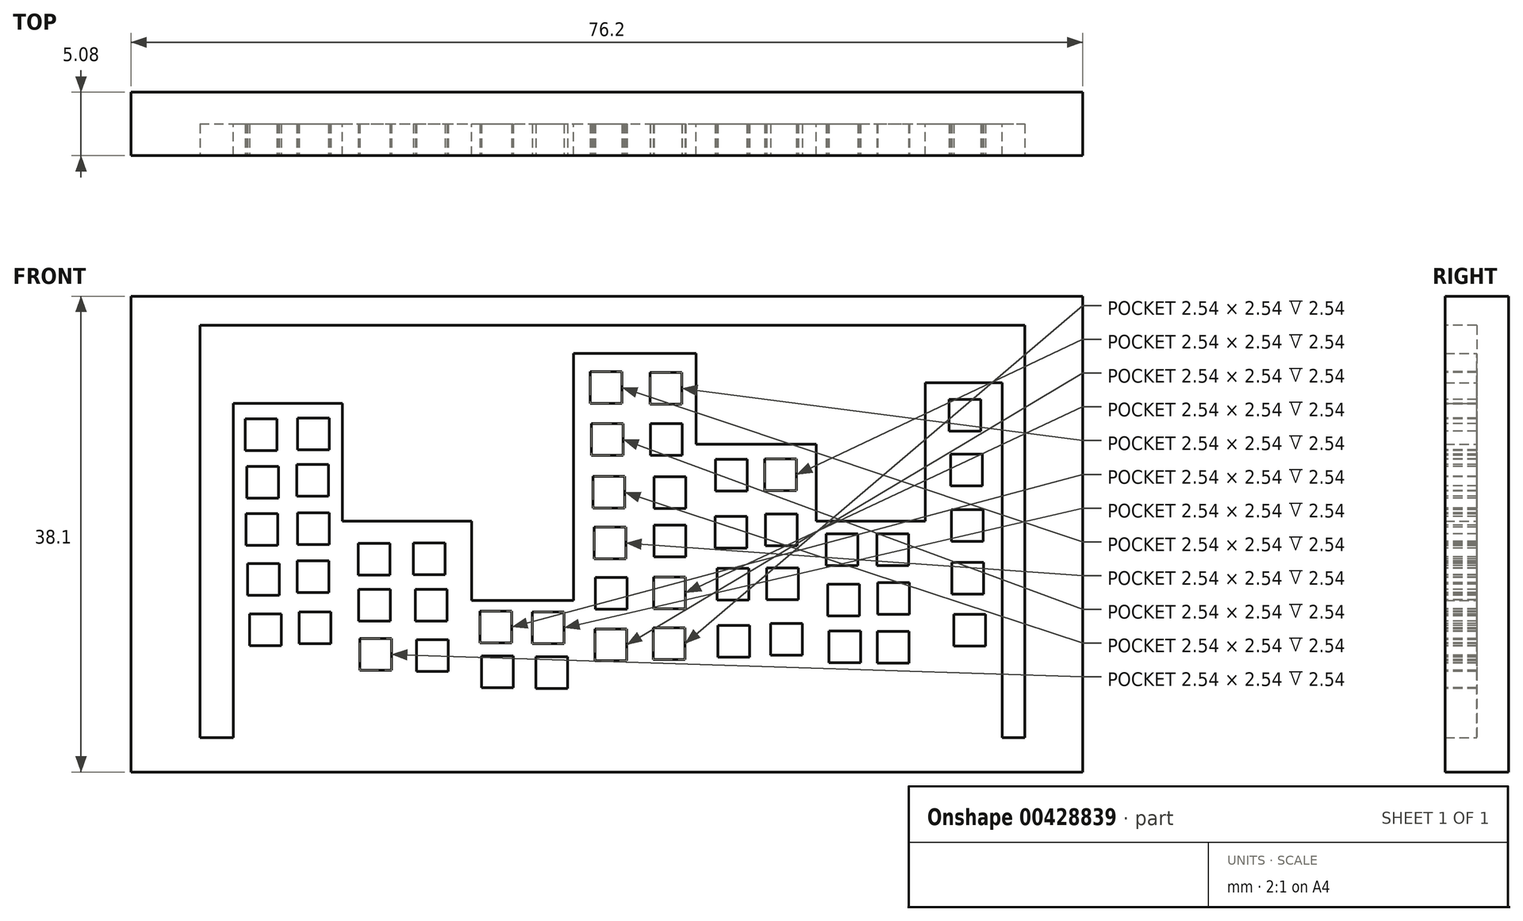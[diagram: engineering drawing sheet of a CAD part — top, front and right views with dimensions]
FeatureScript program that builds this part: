
annotation { "Feature Type Name" : "Feature", "Feature Type Description" : "" }
export const myFeature = defineFeature(function(context is Context, id is Id, definition is map)
    precondition{}
    {
        {
            var Q0;
            Q0=qCreatedBy(makeId("Front.planeOp"),FACE);
            var sketch = newSketch(context, id + "F0", { "sketchPlane" : qUnion([Q0])});
            skLineSegment(sketch, "E0.bottom", {"start": v(0, 0) * mm, "end": v(76.2, 0) * mm});
            skLineSegment(sketch, "E0.top", {"start": v(0, -38.1) * mm, "end": v(76.2, -38.1) * mm});
            skLineSegment(sketch, "E0.left", {"start": v(0, 0) * mm, "end": v(0, -38.1) * mm});
            skLineSegment(sketch, "E0.right", {"start": v(76.2, 0) * mm, "end": v(76.2, -38.1) * mm});
            skSolve(sketch);
        }
        {
            var Q0;
            Q0 = qSketchRegion(id + "F0", true);
            extrude(context, id + "F1", {"entities" : qUnion([Q0]), "depth" : 5.08 * mm});
        }
        {
            var Q0;
            Q0=makeQuery(id+"F1.opExtrude","CAP_FACE",FACE,{"disambiguationData":[OSD([sQuery(id+"F0.wireOp",EDGE,"E0.bottom"),sQuery(id+"F0.wireOp",EDGE,"E0.top"),sQuery(id+"F0.wireOp",EDGE,"E0.left"),sQuery(id+"F0.wireOp",EDGE,"E0.right")])],"isStart":false});
            var sketch = newSketch(context, id + "F2", { "sketchPlane" : qUnion([Q0])});
            skLineSegment(sketch, "E1.bottom", {"start": v(5.51, -2.33) * mm, "end": v(71.55, -2.33) * mm});
            skLineSegment(sketch, "E1.top", {"start": v(5.51, -35.35) * mm, "end": v(71.55, -35.35) * mm});
            skLineSegment(sketch, "E1.left", {"start": v(5.51, -2.33) * mm, "end": v(5.51, -35.35) * mm});
            skLineSegment(sketch, "E1.right", {"start": v(71.55, -2.33) * mm, "end": v(71.55, -35.35) * mm});
            skSolve(sketch);
        }
        {
            var Q0;
            Q0 = qSketchRegion(id + "F2", true);
            extrude(context, id + "F3", {"entities" : qUnion([Q0]), "operationType" : NewBodyOperationType.REMOVE, "oppositeDirection" : true, "depth" : 2.54 * mm});
        }
        {
            var Q0;
            Q0=makeQuery(id+"F3.boolean.opBoolean","COPY",FACE,{"derivedFrom":makeQuery(id+"F3.opExtrude","CAP_FACE",FACE,{"disambiguationData":[OSD([sQuery(id+"F2.wireOp",EDGE,"E1.bottom"),sQuery(id+"F2.wireOp",EDGE,"E1.top"),sQuery(id+"F2.wireOp",EDGE,"E1.left"),sQuery(id+"F2.wireOp",EDGE,"E1.right")])],"isStart":false})});
            var sketch = newSketch(context, id + "F4", { "sketchPlane" : qUnion([Q0])});
            skLineSegment(sketch, "E2.bottom", {"start": v(8.2, -35.35) * mm, "end": v(16.9, -35.35) * mm});
            skLineSegment(sketch, "E2.top", {"start": v(8.2, -8.57) * mm, "end": v(16.9, -8.57) * mm});
            skLineSegment(sketch, "E2.left", {"start": v(8.2, -35.35) * mm, "end": v(8.2, -8.57) * mm});
            skLineSegment(sketch, "E2.right", {"start": v(16.9, -35.35) * mm, "end": v(16.9, -8.57) * mm});
            skLineSegment(sketch, "E3.bottom", {"start": v(16.9, -18.01) * mm, "end": v(27.26, -18.01) * mm});
            skLineSegment(sketch, "E3.top", {"start": v(16.9, -35.35) * mm, "end": v(27.26, -35.35) * mm});
            skLineSegment(sketch, "E3.left", {"start": v(16.9, -18.01) * mm, "end": v(16.9, -35.35) * mm});
            skLineSegment(sketch, "E3.right", {"start": v(27.26, -18.01) * mm, "end": v(27.26, -35.35) * mm});
            skLineSegment(sketch, "E4.bottom", {"start": v(27.26, -24.37) * mm, "end": v(35.43, -24.37) * mm});
            skLineSegment(sketch, "E4.top", {"start": v(27.26, -35.35) * mm, "end": v(35.43, -35.35) * mm});
            skLineSegment(sketch, "E4.left", {"start": v(27.26, -24.37) * mm, "end": v(27.26, -35.35) * mm});
            skLineSegment(sketch, "E4.right", {"start": v(35.43, -24.37) * mm, "end": v(35.43, -35.35) * mm});
            skLineSegment(sketch, "E5.bottom", {"start": v(35.43, -35.35) * mm, "end": v(45.24, -35.35) * mm});
            skLineSegment(sketch, "E5.top", {"start": v(35.43, -4.57) * mm, "end": v(45.24, -4.57) * mm});
            skLineSegment(sketch, "E5.left", {"start": v(35.43, -35.35) * mm, "end": v(35.43, -4.57) * mm});
            skLineSegment(sketch, "E5.right", {"start": v(45.24, -35.35) * mm, "end": v(45.24, -4.57) * mm});
            skLineSegment(sketch, "E6.bottom", {"start": v(45.24, -35.35) * mm, "end": v(54.86, -35.35) * mm});
            skLineSegment(sketch, "E6.top", {"start": v(45.24, -11.84) * mm, "end": v(54.86, -11.84) * mm});
            skLineSegment(sketch, "E6.left", {"start": v(45.24, -35.35) * mm, "end": v(45.24, -11.84) * mm});
            skLineSegment(sketch, "E6.right", {"start": v(54.86, -35.35) * mm, "end": v(54.86, -11.84) * mm});
            skLineSegment(sketch, "E7.bottom", {"start": v(54.86, -35.35) * mm, "end": v(63.58, -35.35) * mm});
            skLineSegment(sketch, "E7.top", {"start": v(54.86, -18.01) * mm, "end": v(63.58, -18.01) * mm});
            skLineSegment(sketch, "E7.left", {"start": v(54.86, -35.35) * mm, "end": v(54.86, -18.01) * mm});
            skLineSegment(sketch, "E7.right", {"start": v(63.58, -35.35) * mm, "end": v(63.58, -18.01) * mm});
            skLineSegment(sketch, "E8.bottom", {"start": v(63.58, -35.35) * mm, "end": v(69.75, -35.35) * mm});
            skLineSegment(sketch, "E8.top", {"start": v(63.58, -6.93) * mm, "end": v(69.75, -6.93) * mm});
            skLineSegment(sketch, "E8.left", {"start": v(63.58, -35.35) * mm, "end": v(63.58, -6.93) * mm});
            skLineSegment(sketch, "E8.right", {"start": v(69.75, -35.35) * mm, "end": v(69.75, -6.93) * mm});
            skSolve(sketch);
        }
        {
            var Q0;
            Q0 = qSketchRegion(id + "F4", true);
            extrude(context, id + "F5", {"entities" : qUnion([Q0]), "operationType" : NewBodyOperationType.ADD, "depth" : 2.54 * mm});
        }
        {
            var Q0;
            Q0=makeQuery(id+"F5.boolean.opBoolean","MERGE",FACE,{"derivedFrom":[makeQuery(id+"F1.opExtrude","CAP_FACE",FACE,{"disambiguationData":[OSD([sQuery(id+"F0.wireOp",EDGE,"E0.bottom"),sQuery(id+"F0.wireOp",EDGE,"E0.top"),sQuery(id+"F0.wireOp",EDGE,"E0.left"),sQuery(id+"F0.wireOp",EDGE,"E0.right")])],"isStart":false}),makeQuery(id+"F5.opExtrude","CAP_FACE",FACE,{"disambiguationData":[OSD([sQuery(id+"F4.wireOp",EDGE,"E2.bottom"),sQuery(id+"F4.wireOp",EDGE,"E2.top"),sQuery(id+"F4.wireOp",EDGE,"E2.left"),sQuery(id+"F4.wireOp",EDGE,"E2.right"),sQuery(id+"F4.wireOp",EDGE,"E3.bottom"),sQuery(id+"F4.wireOp",EDGE,"E3.top"),sQuery(id+"F4.wireOp",EDGE,"E3.right"),sQuery(id+"F4.wireOp",EDGE,"E4.bottom"),sQuery(id+"F4.wireOp",EDGE,"E4.top"),sQuery(id+"F4.wireOp",EDGE,"E5.bottom"),sQuery(id+"F4.wireOp",EDGE,"E5.top"),sQuery(id+"F4.wireOp",EDGE,"E5.left"),sQuery(id+"F4.wireOp",EDGE,"E5.right"),sQuery(id+"F4.wireOp",EDGE,"E6.bottom"),sQuery(id+"F4.wireOp",EDGE,"E6.top"),sQuery(id+"F4.wireOp",EDGE,"E6.right"),sQuery(id+"F4.wireOp",EDGE,"E7.bottom"),sQuery(id+"F4.wireOp",EDGE,"E7.top"),sQuery(id+"F4.wireOp",EDGE,"E8.bottom"),sQuery(id+"F4.wireOp",EDGE,"E8.top"),sQuery(id+"F4.wireOp",EDGE,"E8.left"),sQuery(id+"F4.wireOp",EDGE,"E8.right")])],"isStart":false})]});
            var sketch = newSketch(context, id + "F6", { "sketchPlane" : qUnion([Q0])});
            skLineSegment(sketch, "E9.bottom", {"start": v(9.16, -9.81) * mm, "end": v(11.7, -9.81) * mm});
            skLineSegment(sketch, "E9.top", {"start": v(9.16, -12.35) * mm, "end": v(11.7, -12.35) * mm});
            skLineSegment(sketch, "E9.left", {"start": v(9.16, -9.81) * mm, "end": v(9.16, -12.35) * mm});
            skLineSegment(sketch, "E9.right", {"start": v(11.7, -9.81) * mm, "end": v(11.7, -12.35) * mm});
            skLineSegment(sketch, "E10.bottom", {"start": v(13.35, -9.76) * mm, "end": v(15.89, -9.76) * mm});
            skLineSegment(sketch, "E10.top", {"start": v(13.35, -12.3) * mm, "end": v(15.89, -12.3) * mm});
            skLineSegment(sketch, "E10.left", {"start": v(13.35, -9.76) * mm, "end": v(13.35, -12.3) * mm});
            skLineSegment(sketch, "E10.right", {"start": v(15.89, -9.76) * mm, "end": v(15.89, -12.3) * mm});
            skLineSegment(sketch, "E11.bottom", {"start": v(9.28, -13.62) * mm, "end": v(11.82, -13.62) * mm});
            skLineSegment(sketch, "E11.top", {"start": v(9.28, -16.16) * mm, "end": v(11.82, -16.16) * mm});
            skLineSegment(sketch, "E11.left", {"start": v(9.28, -13.62) * mm, "end": v(9.28, -16.16) * mm});
            skLineSegment(sketch, "E11.right", {"start": v(11.82, -13.62) * mm, "end": v(11.82, -16.16) * mm});
            skLineSegment(sketch, "E12.bottom", {"start": v(13.28, -13.49) * mm, "end": v(15.82, -13.49) * mm});
            skLineSegment(sketch, "E12.top", {"start": v(13.28, -16.03) * mm, "end": v(15.82, -16.03) * mm});
            skLineSegment(sketch, "E12.left", {"start": v(13.28, -13.49) * mm, "end": v(13.28, -16.03) * mm});
            skLineSegment(sketch, "E12.right", {"start": v(15.82, -13.49) * mm, "end": v(15.82, -16.03) * mm});
            skLineSegment(sketch, "E13.bottom", {"start": v(9.2, -17.42) * mm, "end": v(11.74, -17.42) * mm});
            skLineSegment(sketch, "E13.top", {"start": v(9.2, -19.96) * mm, "end": v(11.74, -19.96) * mm});
            skLineSegment(sketch, "E13.left", {"start": v(9.2, -17.42) * mm, "end": v(9.2, -19.96) * mm});
            skLineSegment(sketch, "E13.right", {"start": v(11.74, -17.42) * mm, "end": v(11.74, -19.96) * mm});
            skLineSegment(sketch, "E14.bottom", {"start": v(13.35, -17.36) * mm, "end": v(15.89, -17.36) * mm});
            skLineSegment(sketch, "E14.top", {"start": v(13.35, -19.9) * mm, "end": v(15.89, -19.9) * mm});
            skLineSegment(sketch, "E14.left", {"start": v(13.35, -17.36) * mm, "end": v(13.35, -19.9) * mm});
            skLineSegment(sketch, "E14.right", {"start": v(15.89, -17.36) * mm, "end": v(15.89, -19.9) * mm});
            skLineSegment(sketch, "E15.bottom", {"start": v(9.33, -21.4) * mm, "end": v(11.87, -21.4) * mm});
            skLineSegment(sketch, "E15.top", {"start": v(9.33, -23.95) * mm, "end": v(11.87, -23.95) * mm});
            skLineSegment(sketch, "E15.left", {"start": v(9.33, -21.4) * mm, "end": v(9.33, -23.95) * mm});
            skLineSegment(sketch, "E15.right", {"start": v(11.87, -21.4) * mm, "end": v(11.87, -23.95) * mm});
            skLineSegment(sketch, "E16.bottom", {"start": v(13.29, -21.18) * mm, "end": v(15.83, -21.18) * mm});
            skLineSegment(sketch, "E16.top", {"start": v(13.29, -23.72) * mm, "end": v(15.83, -23.72) * mm});
            skLineSegment(sketch, "E16.left", {"start": v(13.29, -21.18) * mm, "end": v(13.29, -23.72) * mm});
            skLineSegment(sketch, "E16.right", {"start": v(15.83, -21.18) * mm, "end": v(15.83, -23.72) * mm});
            skLineSegment(sketch, "E17.bottom", {"start": v(18.19, -19.78) * mm, "end": v(20.73, -19.78) * mm});
            skLineSegment(sketch, "E17.top", {"start": v(18.19, -22.32) * mm, "end": v(20.73, -22.32) * mm});
            skLineSegment(sketch, "E17.left", {"start": v(18.19, -19.78) * mm, "end": v(18.19, -22.32) * mm});
            skLineSegment(sketch, "E17.right", {"start": v(20.73, -19.78) * mm, "end": v(20.73, -22.32) * mm});
            skLineSegment(sketch, "E18.bottom", {"start": v(22.62, -19.75) * mm, "end": v(25.16, -19.75) * mm});
            skLineSegment(sketch, "E18.top", {"start": v(22.62, -22.29) * mm, "end": v(25.16, -22.29) * mm});
            skLineSegment(sketch, "E18.left", {"start": v(22.62, -19.75) * mm, "end": v(22.62, -22.29) * mm});
            skLineSegment(sketch, "E18.right", {"start": v(25.16, -19.75) * mm, "end": v(25.16, -22.29) * mm});
            skLineSegment(sketch, "E19.bottom", {"start": v(18.24, -23.46) * mm, "end": v(20.78, -23.46) * mm});
            skLineSegment(sketch, "E19.top", {"start": v(18.24, -26) * mm, "end": v(20.78, -26) * mm});
            skLineSegment(sketch, "E19.left", {"start": v(18.24, -23.46) * mm, "end": v(18.24, -26) * mm});
            skLineSegment(sketch, "E19.right", {"start": v(20.78, -23.46) * mm, "end": v(20.78, -26) * mm});
            skLineSegment(sketch, "E20.bottom", {"start": v(22.75, -23.47) * mm, "end": v(25.3, -23.47) * mm});
            skLineSegment(sketch, "E20.top", {"start": v(22.75, -26) * mm, "end": v(25.3, -26) * mm});
            skLineSegment(sketch, "E20.left", {"start": v(22.75, -23.47) * mm, "end": v(22.75, -26) * mm});
            skLineSegment(sketch, "E20.right", {"start": v(25.3, -23.47) * mm, "end": v(25.3, -26) * mm});
            skLineSegment(sketch, "E21.bottom", {"start": v(9.5, -25.45) * mm, "end": v(12.03, -25.45) * mm});
            skLineSegment(sketch, "E21.top", {"start": v(9.5, -28) * mm, "end": v(12.03, -28) * mm});
            skLineSegment(sketch, "E21.left", {"start": v(9.5, -25.45) * mm, "end": v(9.5, -28) * mm});
            skLineSegment(sketch, "E21.right", {"start": v(12.03, -25.45) * mm, "end": v(12.03, -28) * mm});
            skLineSegment(sketch, "E22.bottom", {"start": v(13.45, -25.28) * mm, "end": v(16, -25.28) * mm});
            skLineSegment(sketch, "E22.top", {"start": v(13.45, -27.82) * mm, "end": v(16, -27.82) * mm});
            skLineSegment(sketch, "E22.left", {"start": v(13.45, -25.28) * mm, "end": v(13.45, -27.82) * mm});
            skLineSegment(sketch, "E22.right", {"start": v(16, -25.28) * mm, "end": v(16, -27.82) * mm});
            skLineSegment(sketch, "E23.bottom", {"start": v(22.86, -27.5) * mm, "end": v(25.4, -27.5) * mm});
            skLineSegment(sketch, "E23.top", {"start": v(22.86, -30.05) * mm, "end": v(25.4, -30.05) * mm});
            skLineSegment(sketch, "E23.left", {"start": v(22.86, -27.5) * mm, "end": v(22.86, -30.05) * mm});
            skLineSegment(sketch, "E23.right", {"start": v(25.4, -27.5) * mm, "end": v(25.4, -30.05) * mm});
            skLineSegment(sketch, "E24.bottom", {"start": v(28.08, -28.8) * mm, "end": v(30.62, -28.8) * mm});
            skLineSegment(sketch, "E24.top", {"start": v(28.08, -31.34) * mm, "end": v(30.62, -31.34) * mm});
            skLineSegment(sketch, "E24.left", {"start": v(28.08, -28.8) * mm, "end": v(28.08, -31.34) * mm});
            skLineSegment(sketch, "E24.right", {"start": v(30.62, -28.8) * mm, "end": v(30.62, -31.34) * mm});
            skLineSegment(sketch, "E25.bottom", {"start": v(32.43, -28.87) * mm, "end": v(34.97, -28.87) * mm});
            skLineSegment(sketch, "E25.top", {"start": v(32.43, -31.41) * mm, "end": v(34.97, -31.41) * mm});
            skLineSegment(sketch, "E25.left", {"start": v(32.43, -28.87) * mm, "end": v(32.43, -31.41) * mm});
            skLineSegment(sketch, "E25.right", {"start": v(34.97, -28.87) * mm, "end": v(34.97, -31.41) * mm});
            skLineSegment(sketch, "E26.bottom", {"start": v(36.76, -6.04) * mm, "end": v(39.3, -6.04) * mm});
            skLineSegment(sketch, "E26.top", {"start": v(36.76, -8.58) * mm, "end": v(39.3, -8.58) * mm});
            skLineSegment(sketch, "E26.left", {"start": v(36.76, -6.04) * mm, "end": v(36.76, -8.58) * mm});
            skLineSegment(sketch, "E26.right", {"start": v(39.3, -6.04) * mm, "end": v(39.3, -8.58) * mm});
            skLineSegment(sketch, "E27.bottom", {"start": v(32.13, -25.3) * mm, "end": v(34.67, -25.3) * mm});
            skLineSegment(sketch, "E27.top", {"start": v(32.13, -27.84) * mm, "end": v(34.67, -27.84) * mm});
            skLineSegment(sketch, "E27.left", {"start": v(32.13, -25.3) * mm, "end": v(32.13, -27.84) * mm});
            skLineSegment(sketch, "E27.right", {"start": v(34.67, -25.3) * mm, "end": v(34.67, -27.84) * mm});
            skLineSegment(sketch, "E28.bottom", {"start": v(27.94, -25.23) * mm, "end": v(30.48, -25.23) * mm});
            skLineSegment(sketch, "E28.top", {"start": v(27.94, -27.77) * mm, "end": v(30.48, -27.77) * mm});
            skLineSegment(sketch, "E28.left", {"start": v(27.94, -25.23) * mm, "end": v(27.94, -27.77) * mm});
            skLineSegment(sketch, "E28.right", {"start": v(30.48, -25.23) * mm, "end": v(30.48, -27.77) * mm});
            skLineSegment(sketch, "E29.bottom", {"start": v(41.56, -6.1) * mm, "end": v(44.1, -6.1) * mm});
            skLineSegment(sketch, "E29.top", {"start": v(41.56, -8.64) * mm, "end": v(44.1, -8.64) * mm});
            skLineSegment(sketch, "E29.left", {"start": v(41.56, -6.1) * mm, "end": v(41.56, -8.64) * mm});
            skLineSegment(sketch, "E29.right", {"start": v(44.1, -6.1) * mm, "end": v(44.1, -8.64) * mm});
            skLineSegment(sketch, "E30.bottom", {"start": v(18.32, -27.4) * mm, "end": v(20.86, -27.4) * mm});
            skLineSegment(sketch, "E30.top", {"start": v(18.32, -29.94) * mm, "end": v(20.86, -29.94) * mm});
            skLineSegment(sketch, "E30.left", {"start": v(18.32, -27.4) * mm, "end": v(18.32, -29.94) * mm});
            skLineSegment(sketch, "E30.right", {"start": v(20.86, -27.4) * mm, "end": v(20.86, -29.94) * mm});
            skLineSegment(sketch, "E31.bottom", {"start": v(37, -14.42) * mm, "end": v(39.53, -14.42) * mm});
            skLineSegment(sketch, "E31.top", {"start": v(37, -16.96) * mm, "end": v(39.53, -16.96) * mm});
            skLineSegment(sketch, "E31.left", {"start": v(37, -14.42) * mm, "end": v(37, -16.96) * mm});
            skLineSegment(sketch, "E31.right", {"start": v(39.53, -14.42) * mm, "end": v(39.53, -16.96) * mm});
            skLineSegment(sketch, "E32.bottom", {"start": v(36.85, -10.19) * mm, "end": v(39.4, -10.19) * mm});
            skLineSegment(sketch, "E32.top", {"start": v(36.85, -12.73) * mm, "end": v(39.4, -12.73) * mm});
            skLineSegment(sketch, "E32.left", {"start": v(36.85, -10.19) * mm, "end": v(36.85, -12.73) * mm});
            skLineSegment(sketch, "E32.right", {"start": v(39.4, -10.19) * mm, "end": v(39.4, -12.73) * mm});
            skLineSegment(sketch, "E33.bottom", {"start": v(37.07, -18.5) * mm, "end": v(39.61, -18.5) * mm});
            skLineSegment(sketch, "E33.top", {"start": v(37.07, -21.04) * mm, "end": v(39.61, -21.04) * mm});
            skLineSegment(sketch, "E33.left", {"start": v(37.07, -18.5) * mm, "end": v(37.07, -21.04) * mm});
            skLineSegment(sketch, "E33.right", {"start": v(39.61, -18.5) * mm, "end": v(39.61, -21.04) * mm});
            skLineSegment(sketch, "E34.bottom", {"start": v(41.88, -18.34) * mm, "end": v(44.42, -18.34) * mm});
            skLineSegment(sketch, "E34.top", {"start": v(41.88, -20.88) * mm, "end": v(44.42, -20.88) * mm});
            skLineSegment(sketch, "E34.left", {"start": v(41.88, -18.34) * mm, "end": v(41.88, -20.88) * mm});
            skLineSegment(sketch, "E34.right", {"start": v(44.42, -18.34) * mm, "end": v(44.42, -20.88) * mm});
            skLineSegment(sketch, "E35.bottom", {"start": v(37.2, -22.54) * mm, "end": v(39.73, -22.54) * mm});
            skLineSegment(sketch, "E35.top", {"start": v(37.2, -25.08) * mm, "end": v(39.73, -25.08) * mm});
            skLineSegment(sketch, "E35.left", {"start": v(37.2, -22.54) * mm, "end": v(37.2, -25.08) * mm});
            skLineSegment(sketch, "E35.right", {"start": v(39.73, -22.54) * mm, "end": v(39.73, -25.08) * mm});
            skLineSegment(sketch, "E36.bottom", {"start": v(41.6, -10.21) * mm, "end": v(44.13, -10.21) * mm});
            skLineSegment(sketch, "E36.top", {"start": v(41.6, -12.75) * mm, "end": v(44.13, -12.75) * mm});
            skLineSegment(sketch, "E36.left", {"start": v(41.6, -10.21) * mm, "end": v(41.6, -12.75) * mm});
            skLineSegment(sketch, "E36.right", {"start": v(44.13, -10.21) * mm, "end": v(44.13, -12.75) * mm});
            skLineSegment(sketch, "E37.bottom", {"start": v(41.87, -14.45) * mm, "end": v(44.41, -14.45) * mm});
            skLineSegment(sketch, "E37.top", {"start": v(41.87, -16.99) * mm, "end": v(44.41, -16.99) * mm});
            skLineSegment(sketch, "E37.left", {"start": v(41.87, -14.45) * mm, "end": v(41.87, -16.99) * mm});
            skLineSegment(sketch, "E37.right", {"start": v(44.41, -14.45) * mm, "end": v(44.41, -16.99) * mm});
            skLineSegment(sketch, "E38.bottom", {"start": v(41.86, -22.48) * mm, "end": v(44.4, -22.48) * mm});
            skLineSegment(sketch, "E38.top", {"start": v(41.86, -25.02) * mm, "end": v(44.4, -25.02) * mm});
            skLineSegment(sketch, "E38.left", {"start": v(41.86, -22.48) * mm, "end": v(41.86, -25.02) * mm});
            skLineSegment(sketch, "E38.right", {"start": v(44.4, -22.48) * mm, "end": v(44.4, -25.02) * mm});
            skLineSegment(sketch, "E39.bottom", {"start": v(37.13, -26.63) * mm, "end": v(39.67, -26.63) * mm});
            skLineSegment(sketch, "E39.top", {"start": v(37.13, -29.17) * mm, "end": v(39.67, -29.17) * mm});
            skLineSegment(sketch, "E39.left", {"start": v(37.13, -26.63) * mm, "end": v(37.13, -29.17) * mm});
            skLineSegment(sketch, "E39.right", {"start": v(39.67, -26.63) * mm, "end": v(39.67, -29.17) * mm});
            skLineSegment(sketch, "E40.bottom", {"start": v(50.74, -13.02) * mm, "end": v(53.28, -13.02) * mm});
            skLineSegment(sketch, "E40.top", {"start": v(50.74, -15.56) * mm, "end": v(53.28, -15.56) * mm});
            skLineSegment(sketch, "E40.left", {"start": v(50.74, -13.02) * mm, "end": v(50.74, -15.56) * mm});
            skLineSegment(sketch, "E40.right", {"start": v(53.28, -13.02) * mm, "end": v(53.28, -15.56) * mm});
            skLineSegment(sketch, "E41.bottom", {"start": v(41.83, -26.55) * mm, "end": v(44.37, -26.55) * mm});
            skLineSegment(sketch, "E41.top", {"start": v(41.83, -29.1) * mm, "end": v(44.37, -29.1) * mm});
            skLineSegment(sketch, "E41.left", {"start": v(41.83, -26.55) * mm, "end": v(41.83, -29.1) * mm});
            skLineSegment(sketch, "E41.right", {"start": v(44.37, -26.55) * mm, "end": v(44.37, -29.1) * mm});
            skLineSegment(sketch, "E42.bottom", {"start": v(46.8, -13.06) * mm, "end": v(49.34, -13.06) * mm});
            skLineSegment(sketch, "E42.top", {"start": v(46.8, -15.6) * mm, "end": v(49.34, -15.6) * mm});
            skLineSegment(sketch, "E42.left", {"start": v(46.8, -13.06) * mm, "end": v(46.8, -15.6) * mm});
            skLineSegment(sketch, "E42.right", {"start": v(49.34, -13.06) * mm, "end": v(49.34, -15.6) * mm});
            skLineSegment(sketch, "E43.bottom", {"start": v(50.9, -21.75) * mm, "end": v(53.45, -21.75) * mm});
            skLineSegment(sketch, "E43.top", {"start": v(50.9, -24.3) * mm, "end": v(53.45, -24.3) * mm});
            skLineSegment(sketch, "E43.left", {"start": v(50.9, -21.75) * mm, "end": v(50.9, -24.3) * mm});
            skLineSegment(sketch, "E43.right", {"start": v(53.45, -21.75) * mm, "end": v(53.45, -24.3) * mm});
            skLineSegment(sketch, "E44.bottom", {"start": v(46.92, -21.78) * mm, "end": v(49.46, -21.78) * mm});
            skLineSegment(sketch, "E44.top", {"start": v(46.92, -24.32) * mm, "end": v(49.46, -24.32) * mm});
            skLineSegment(sketch, "E44.left", {"start": v(46.92, -21.78) * mm, "end": v(46.92, -24.32) * mm});
            skLineSegment(sketch, "E44.right", {"start": v(49.46, -21.78) * mm, "end": v(49.46, -24.32) * mm});
            skLineSegment(sketch, "E45.bottom", {"start": v(50.79, -17.45) * mm, "end": v(53.33, -17.45) * mm});
            skLineSegment(sketch, "E45.top", {"start": v(50.79, -19.99) * mm, "end": v(53.33, -19.99) * mm});
            skLineSegment(sketch, "E45.left", {"start": v(50.79, -17.45) * mm, "end": v(50.79, -19.99) * mm});
            skLineSegment(sketch, "E45.right", {"start": v(53.33, -17.45) * mm, "end": v(53.33, -19.99) * mm});
            skLineSegment(sketch, "E46.bottom", {"start": v(46.78, -17.64) * mm, "end": v(49.32, -17.64) * mm});
            skLineSegment(sketch, "E46.top", {"start": v(46.78, -20.18) * mm, "end": v(49.32, -20.18) * mm});
            skLineSegment(sketch, "E46.left", {"start": v(46.78, -17.64) * mm, "end": v(46.78, -20.18) * mm});
            skLineSegment(sketch, "E46.right", {"start": v(49.32, -17.64) * mm, "end": v(49.32, -20.18) * mm});
            skLineSegment(sketch, "E47.bottom", {"start": v(51.2, -26.2) * mm, "end": v(53.74, -26.2) * mm});
            skLineSegment(sketch, "E47.top", {"start": v(51.2, -28.73) * mm, "end": v(53.74, -28.73) * mm});
            skLineSegment(sketch, "E47.left", {"start": v(51.2, -26.2) * mm, "end": v(51.2, -28.73) * mm});
            skLineSegment(sketch, "E47.right", {"start": v(53.74, -26.2) * mm, "end": v(53.74, -28.73) * mm});
            skLineSegment(sketch, "E48.bottom", {"start": v(46.98, -26.38) * mm, "end": v(49.52, -26.38) * mm});
            skLineSegment(sketch, "E48.top", {"start": v(46.98, -28.92) * mm, "end": v(49.52, -28.92) * mm});
            skLineSegment(sketch, "E48.left", {"start": v(46.98, -26.38) * mm, "end": v(46.98, -28.92) * mm});
            skLineSegment(sketch, "E48.right", {"start": v(49.52, -26.38) * mm, "end": v(49.52, -28.92) * mm});
            skLineSegment(sketch, "E49.bottom", {"start": v(55.78, -23.05) * mm, "end": v(58.32, -23.05) * mm});
            skLineSegment(sketch, "E49.top", {"start": v(55.78, -25.6) * mm, "end": v(58.32, -25.6) * mm});
            skLineSegment(sketch, "E49.left", {"start": v(55.78, -23.05) * mm, "end": v(55.78, -25.6) * mm});
            skLineSegment(sketch, "E49.right", {"start": v(58.32, -23.05) * mm, "end": v(58.32, -25.6) * mm});
            skLineSegment(sketch, "E50.bottom", {"start": v(59.71, -19.02) * mm, "end": v(62.25, -19.02) * mm});
            skLineSegment(sketch, "E50.top", {"start": v(59.71, -21.56) * mm, "end": v(62.25, -21.56) * mm});
            skLineSegment(sketch, "E50.left", {"start": v(59.71, -19.02) * mm, "end": v(59.71, -21.56) * mm});
            skLineSegment(sketch, "E50.right", {"start": v(62.25, -19.02) * mm, "end": v(62.25, -21.56) * mm});
            skLineSegment(sketch, "E51.bottom", {"start": v(55.66, -19.03) * mm, "end": v(58.2, -19.03) * mm});
            skLineSegment(sketch, "E51.top", {"start": v(55.66, -21.57) * mm, "end": v(58.2, -21.57) * mm});
            skLineSegment(sketch, "E51.left", {"start": v(55.66, -19.03) * mm, "end": v(55.66, -21.57) * mm});
            skLineSegment(sketch, "E51.right", {"start": v(58.2, -19.03) * mm, "end": v(58.2, -21.57) * mm});
            skLineSegment(sketch, "E52.bottom", {"start": v(55.87, -26.82) * mm, "end": v(58.41, -26.82) * mm});
            skLineSegment(sketch, "E52.top", {"start": v(55.87, -29.36) * mm, "end": v(58.41, -29.36) * mm});
            skLineSegment(sketch, "E52.left", {"start": v(55.87, -26.82) * mm, "end": v(55.87, -29.36) * mm});
            skLineSegment(sketch, "E52.right", {"start": v(58.41, -26.82) * mm, "end": v(58.41, -29.36) * mm});
            skLineSegment(sketch, "E53.bottom", {"start": v(59.78, -22.94) * mm, "end": v(62.32, -22.94) * mm});
            skLineSegment(sketch, "E53.top", {"start": v(59.78, -25.48) * mm, "end": v(62.32, -25.48) * mm});
            skLineSegment(sketch, "E53.left", {"start": v(59.78, -22.94) * mm, "end": v(59.78, -25.48) * mm});
            skLineSegment(sketch, "E53.right", {"start": v(62.32, -22.94) * mm, "end": v(62.32, -25.48) * mm});
            skLineSegment(sketch, "E54.bottom", {"start": v(59.76, -26.83) * mm, "end": v(62.3, -26.83) * mm});
            skLineSegment(sketch, "E54.top", {"start": v(59.76, -29.37) * mm, "end": v(62.3, -29.37) * mm});
            skLineSegment(sketch, "E54.left", {"start": v(59.76, -26.83) * mm, "end": v(59.76, -29.37) * mm});
            skLineSegment(sketch, "E54.right", {"start": v(62.3, -26.83) * mm, "end": v(62.3, -29.37) * mm});
            skLineSegment(sketch, "E55.bottom", {"start": v(65.48, -8.26) * mm, "end": v(68.02, -8.26) * mm});
            skLineSegment(sketch, "E55.top", {"start": v(65.48, -10.8) * mm, "end": v(68.02, -10.8) * mm});
            skLineSegment(sketch, "E55.left", {"start": v(65.48, -8.26) * mm, "end": v(65.48, -10.8) * mm});
            skLineSegment(sketch, "E55.right", {"start": v(68.02, -8.26) * mm, "end": v(68.02, -10.8) * mm});
            skLineSegment(sketch, "E56.bottom", {"start": v(65.68, -17.1) * mm, "end": v(68.22, -17.1) * mm});
            skLineSegment(sketch, "E56.top", {"start": v(65.68, -19.64) * mm, "end": v(68.22, -19.64) * mm});
            skLineSegment(sketch, "E56.left", {"start": v(65.68, -17.1) * mm, "end": v(65.68, -19.64) * mm});
            skLineSegment(sketch, "E56.right", {"start": v(68.22, -17.1) * mm, "end": v(68.22, -19.64) * mm});
            skLineSegment(sketch, "E57.bottom", {"start": v(65.62, -12.64) * mm, "end": v(68.16, -12.64) * mm});
            skLineSegment(sketch, "E57.top", {"start": v(65.62, -15.18) * mm, "end": v(68.16, -15.18) * mm});
            skLineSegment(sketch, "E57.left", {"start": v(65.62, -12.64) * mm, "end": v(65.62, -15.18) * mm});
            skLineSegment(sketch, "E57.right", {"start": v(68.16, -12.64) * mm, "end": v(68.16, -15.18) * mm});
            skLineSegment(sketch, "E58.bottom", {"start": v(65.87, -25.46) * mm, "end": v(68.4, -25.46) * mm});
            skLineSegment(sketch, "E58.top", {"start": v(65.87, -28) * mm, "end": v(68.4, -28) * mm});
            skLineSegment(sketch, "E58.left", {"start": v(65.87, -25.46) * mm, "end": v(65.87, -28) * mm});
            skLineSegment(sketch, "E58.right", {"start": v(68.4, -25.46) * mm, "end": v(68.4, -28) * mm});
            skLineSegment(sketch, "E59.bottom", {"start": v(65.73, -21.3) * mm, "end": v(68.27, -21.3) * mm});
            skLineSegment(sketch, "E59.top", {"start": v(65.73, -23.84) * mm, "end": v(68.27, -23.84) * mm});
            skLineSegment(sketch, "E59.left", {"start": v(65.73, -21.3) * mm, "end": v(65.73, -23.84) * mm});
            skLineSegment(sketch, "E59.right", {"start": v(68.27, -21.3) * mm, "end": v(68.27, -23.84) * mm});
            skSolve(sketch);
        }
        {
            var Q0;
            Q0 = qSketchRegion(id + "F6", true);
            extrude(context, id + "F7", {"entities" : qUnion([Q0]), "operationType" : NewBodyOperationType.REMOVE, "oppositeDirection" : true, "depth" : 2.54 * mm});
        }
    });
